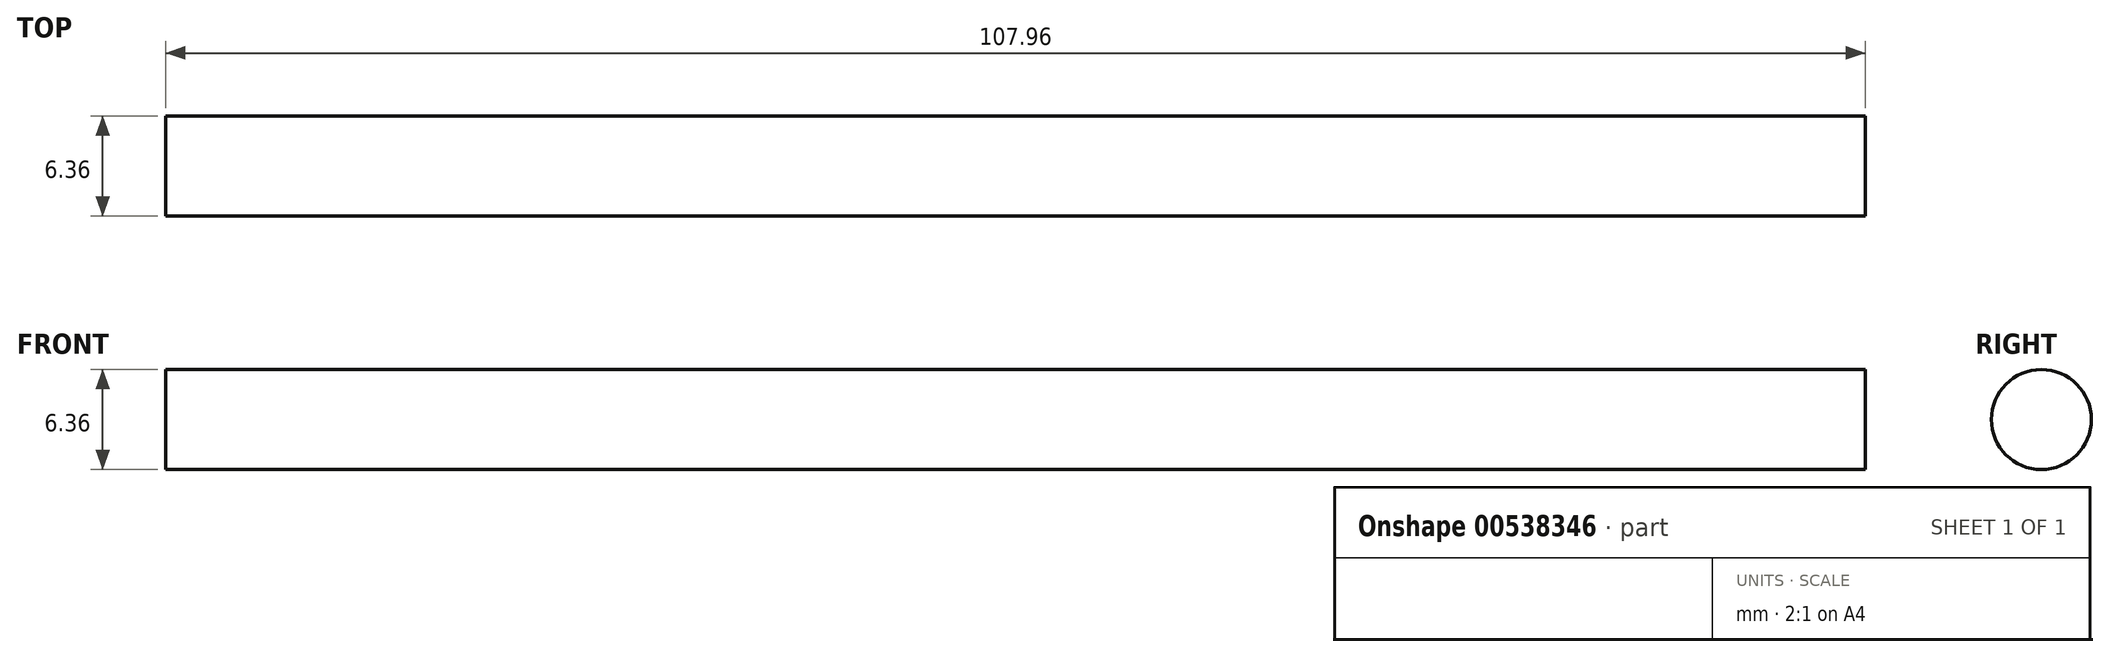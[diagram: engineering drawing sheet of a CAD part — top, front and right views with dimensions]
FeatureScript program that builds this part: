
annotation { "Feature Type Name" : "Feature", "Feature Type Description" : "" }
export const myFeature = defineFeature(function(context is Context, id is Id, definition is map)
    precondition{}
    {
        {
            var Q0;
            Q0=qCreatedBy(makeId("Right.planeOp"),FACE);
            var sketch = newSketch(context, id + "F0", { "sketchPlane" : qUnion([Q0])});
            skCircle(sketch, "E0", {"center": v(0, 0) * mm, "radius": 3.18 * mm});
            skSolve(sketch);
        }
        {
            var Q0;
            Q0 = qSketchRegion(id + "F0", true);
            extrude(context, id + "F1", {"entities" : qUnion([Q0]), "endBound" : BoundingType.SYMMETRIC, "depth" : 107.95 * mm, "offsetDistance" : 25.4 * mm});
        }
    });
